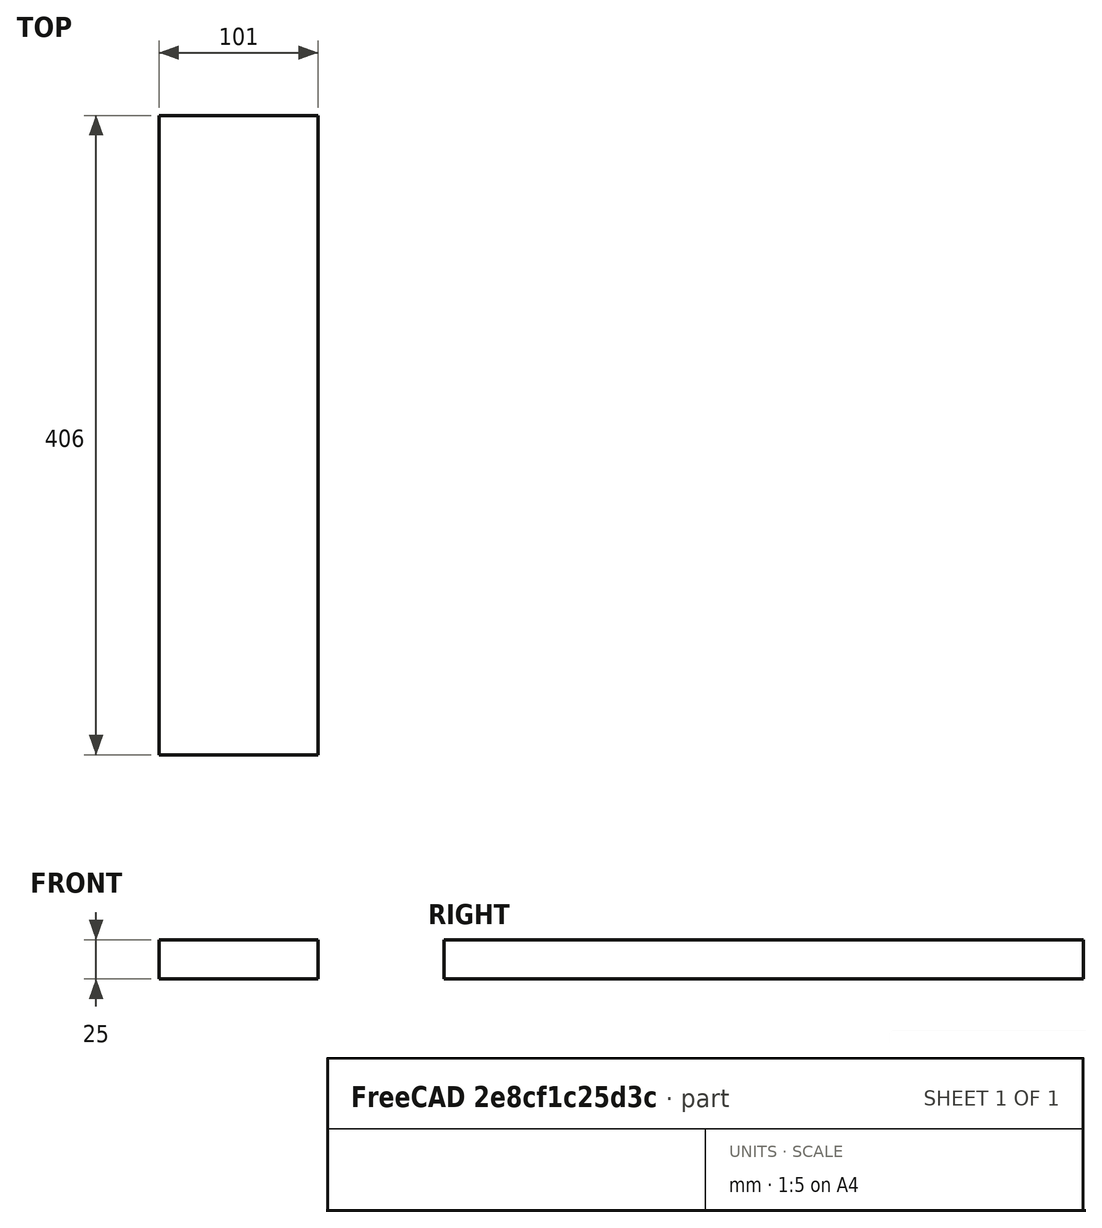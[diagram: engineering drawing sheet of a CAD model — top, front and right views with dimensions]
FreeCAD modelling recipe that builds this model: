
FCSTD DOCUMENT  (FreeCAD 0.19R24276 (Git))
Label: wood seat
License: All rights reserved
LicenseURL: http://en.wikipedia.org/wiki/All_rights_reserved
objects: Sketcher::SketchObject×1, PartDesign::Pad×1, PartDesign::Body×1
note: 4 computed .brp shape members not serialized (recipe doc carries the construction recipe); baked Part::Feature solids carry a one-line shape summary decoded from their .brp

FEATURE [Sketcher::SketchObject] Sketch
  FullyConstrained = true
  MapMode = 5
  Support = -> [XY_Plane]
  sketch-geometry (4):
    g0: LineSegment StartX=0 StartY=0 StartZ=0 EndX=101 EndY=0 EndZ=0
    g1: LineSegment StartX=101 StartY=0 StartZ=0 EndX=101 EndY=406 EndZ=0
    g2: LineSegment StartX=101 StartY=406 StartZ=0 EndX=0 EndY=406 EndZ=0
    g3: LineSegment StartX=0 StartY=406 StartZ=0 EndX=0 EndY=0 EndZ=0
  constraints (11):
    c: Coincident(g0,g1)
    c: Coincident(g1,g2)
    c: Coincident(g2,g3)
    c: Coincident(g3,g0)
    c: Horizontal(g0)
    c: Horizontal(g2)
    c: Vertical(g1)
    c: Vertical(g3)
    c: Coincident(g0,g-1)
    c: DistanceY(g1,g1) = 406
    c: DistanceX(g0,g0) = 101
FEATURE [PartDesign::Pad] Pad
  Direction = (1,1,1)
  Length = 25
  Length2 = 100
  Profile = -> Sketch
  Type = 0
FEATURE [PartDesign::Body] Body
  Group = -> [Sketch,Pad]
  Origin = -> Origin
  Tip = -> Pad
